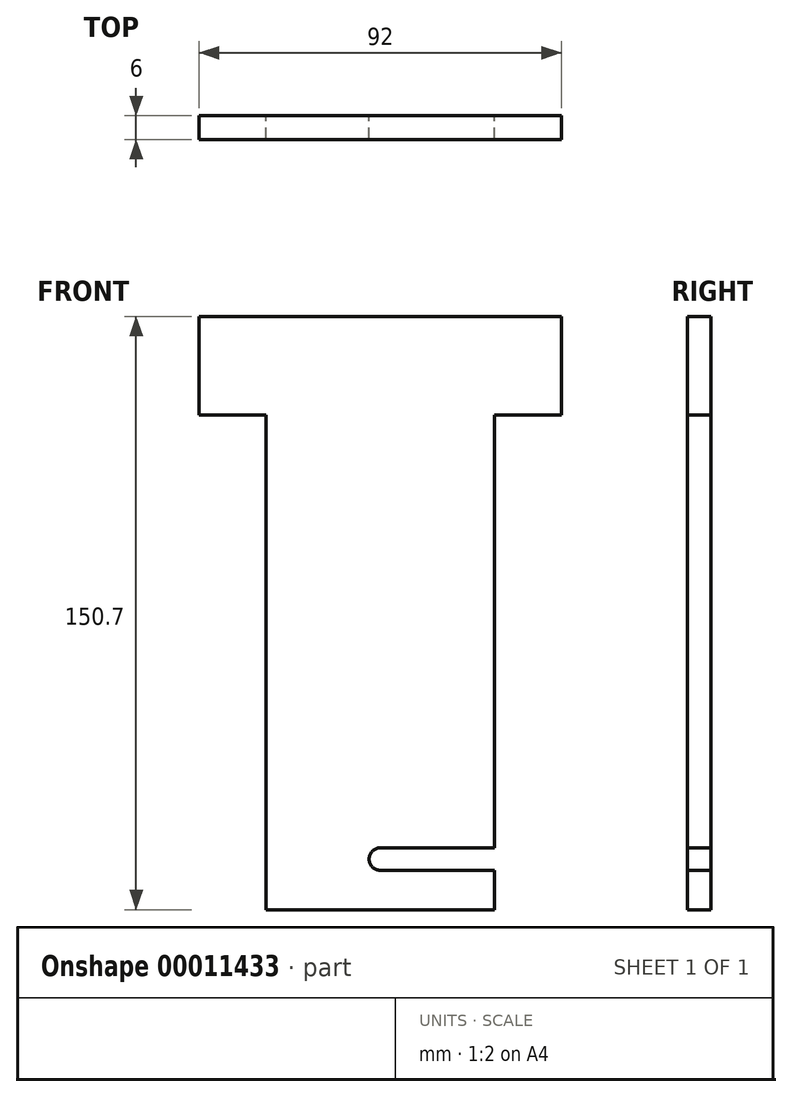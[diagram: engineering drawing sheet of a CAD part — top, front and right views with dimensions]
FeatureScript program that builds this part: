
annotation { "Feature Type Name" : "Feature", "Feature Type Description" : "" }
export const myFeature = defineFeature(function(context is Context, id is Id, definition is map)
    precondition{}
    {
        {
            var Q0;
            Q0=qCreatedBy(makeId("Front.planeOp"),FACE);
            var sketch = newSketch(context, id + "F0", { "sketchPlane" : qUnion([Q0])});
            skLineSegment(sketch, "E0.bottom", {"start": v(-46, 25) * mm, "end": v(46, 25) * mm});
            skLineSegment(sketch, "E0.top", {"start": v(-46, 0) * mm, "end": v(-34.75, 0) * mm});
            skLineSegment(sketch, "E0.left", {"start": v(-46, 25) * mm, "end": v(-46, 0) * mm});
            skLineSegment(sketch, "E0.right", {"start": v(46, 25) * mm, "end": v(46, 0) * mm});
            skLineSegment(sketch, "E1.top", {"start": v(0, -110) * mm, "end": v(29.05, -110) * mm});
            skLineSegment(sketch, "E1.left", {"start": v(-29.05, 0) * mm, "end": v(-29.05, -110) * mm});
            skLineSegment(sketch, "E1.right", {"start": v(29.05, 0) * mm, "end": v(29.05, -110) * mm});
            skLineSegment(sketch, "E2", {"start": v(-34.75, 0) * mm, "end": v(-34.75, 0) * mm});
            skLineSegment(sketch, "E3", {"start": v(-34.75, 0) * mm, "end": v(-29.05, 0) * mm});
            skLineSegment(sketch, "E4", {"start": v(-29.05, 0) * mm, "end": v(-29.05, 0) * mm});
            skLineSegment(sketch, "E5.0.MirrorCS", {"start": v(34.75, 0) * mm, "end": v(29.05, 0) * mm});
            skLineSegment(sketch, "E6.0.MirrorCS", {"start": v(34.75, 0) * mm, "end": v(34.75, 0) * mm});
            skLineSegment(sketch, "E7.0.MirrorCS", {"start": v(29.05, 0) * mm, "end": v(29.05, 0) * mm});
            skLineSegment(sketch, "E8.trimOffspring", {"start": v(34.75, 0) * mm, "end": v(46, 0) * mm});
            skLineSegment(sketch, "E9.top", {"start": v(-29.05, -125.7) * mm, "end": v(29.05, -125.7) * mm});
            skLineSegment(sketch, "E9.left", {"start": v(-29.05, -110) * mm, "end": v(-29.05, -125.7) * mm});
            skLineSegment(sketch, "E9.right", {"start": v(29.05, -115.7) * mm, "end": v(29.05, -125.7) * mm});
            skLineSegment(sketch, "E10", {"start": v(0, -110) * mm, "end": v(0, -115.7) * mm, "construction": true});
            skLineSegment(sketch, "E11", {"start": v(0, -115.7) * mm, "end": v(29.05, -115.7) * mm});
            skArc(sketch, "E12", {"start": v(0, -110) * mm, "mid": v(-2.85, -112.85) * mm, "end": v(0, -115.7) * mm});
            skSolve(sketch);
        }
        {
            var Q0;
            Q0=makeQuery(id+"F0.imprint","IMPRINT",FACE,{"disambiguationData":[TD([[makeQuery(id+"F0.imprint","IMPRINT",EDGE,{"derivedFrom":sQuery(id+"F0.wireOp",EDGE,"E0.bottom")}),-1.0]])]});
            extrude(context, id + "F1", {"entities" : qUnion([Q0]), "depth" : 6 * mm});
        }
    });
